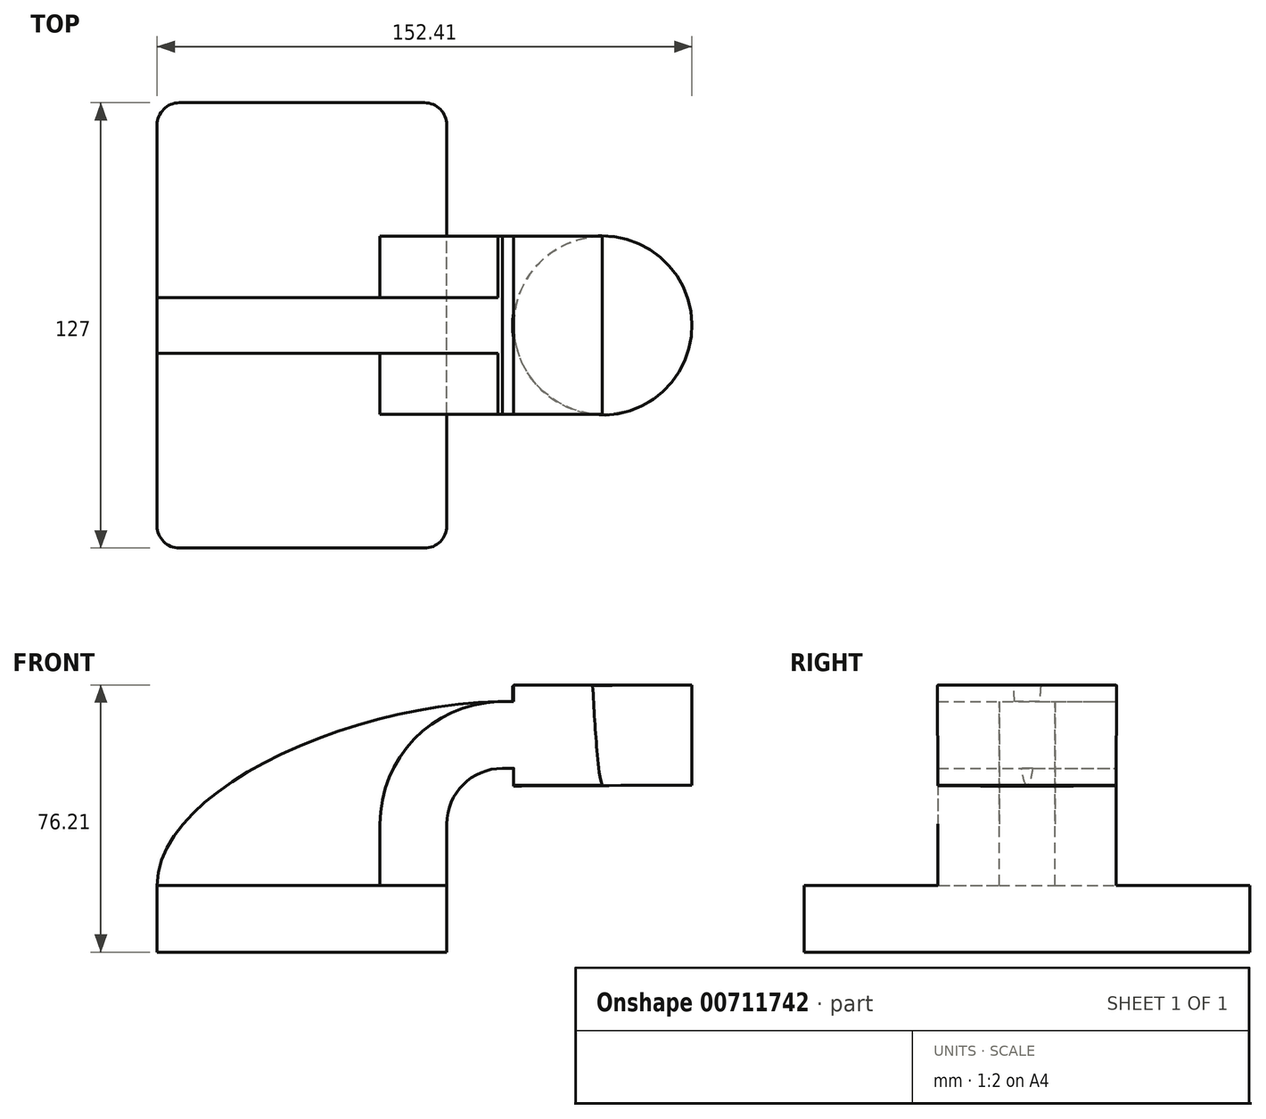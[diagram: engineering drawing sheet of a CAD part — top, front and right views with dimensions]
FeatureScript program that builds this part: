
annotation { "Feature Type Name" : "Feature", "Feature Type Description" : "" }
export const myFeature = defineFeature(function(context is Context, id is Id, definition is map)
    precondition{}
    {
        {
            var Q0;
            Q0=qCreatedBy(makeId("Front.planeOp"),FACE);
            var sketch = newSketch(context, id + "F0", { "sketchPlane" : qUnion([Q0])});
            skLineSegment(sketch, "E0.bottom", {"start": v(-41.28, -9.52) * mm, "end": v(41.28, -9.52) * mm});
            skLineSegment(sketch, "E0.top", {"start": v(-41.28, 9.52) * mm, "end": v(41.28, 9.52) * mm});
            skLineSegment(sketch, "E0.left", {"start": v(-41.28, -9.52) * mm, "end": v(-41.28, 9.52) * mm});
            skLineSegment(sketch, "E0.right", {"start": v(41.28, -9.52) * mm, "end": v(41.28, 9.52) * mm});
            skPoint(sketch, "E0.middle", {"position": v(0, 0) * mm});
            skLineSegment(sketch, "E1.bottom", {"start": v(60.33, 38.1) * mm, "end": v(111.12, 38.1) * mm});
            skLineSegment(sketch, "E1.top", {"start": v(60.33, 66.68) * mm, "end": v(111.12, 66.68) * mm});
            skLineSegment(sketch, "E1.left", {"start": v(60.33, 38.1) * mm, "end": v(60.32, 66.68) * mm});
            skLineSegment(sketch, "E1.right", {"start": v(111.12, 38.1) * mm, "end": v(111.12, 66.68) * mm});
            skPoint(sketch, "E1.middle", {"position": v(85.72, 52.39) * mm});
            skLineSegment(sketch, "E2", {"start": v(41.27, 9.52) * mm, "end": v(41.27, 27) * mm});
            skArc(sketch, "E3", {"start": v(41.27, 27) * mm, "mid": v(45.92, 38.23) * mm, "end": v(57.15, 42.88) * mm});
            skLineSegment(sketch, "E4", {"start": v(57.15, 42.88) * mm, "end": v(85.58, 42.88) * mm});
            skLineSegment(sketch, "E5.0", {"start": v(57.15, 61.93) * mm, "end": v(85.58, 61.93) * mm});
            skArc(sketch, "E5.1", {"start": v(22.23, 27) * mm, "mid": v(32.45, 51.7) * mm, "end": v(57.15, 61.93) * mm});
            skLineSegment(sketch, "E5.2", {"start": v(22.22, 9.52) * mm, "end": v(22.22, 27) * mm});
            skLineSegment(sketch, "E6", {"start": v(85.72, 38.1) * mm, "end": v(85.58, 66.68) * mm});
            skFitSpline(sketch, "E7", {"points": [v(-41.28, 9.53) * mm, v(57.15, 61.93) * mm], "startDerivative": vector(1.41, 83.98) * mm, "endDerivative": vector(126.93, 1.68) * mm});
            skSolve(sketch);
        }
        {
            var Q0;
            Q0=makeQuery(id+"F0.imprint","IMPRINT",FACE,{"disambiguationData":[TD([[makeQuery(id+"F0.imprint","IMPRINT",EDGE,{"derivedFrom":sQuery(id+"F0.wireOp",EDGE,"E0.bottom")}),1.0]])]});
            extrude(context, id + "F1", {"entities" : qUnion([Q0]), "endBound" : BoundingType.SYMMETRIC, "depth" : 127 * mm, "offsetDistance" : 25.4 * mm});
        }
        {
            var Q0;
            {var subQ1=sQuery(id+"F0.wireOp",EDGE,"E2");Q0=makeQuery(id+"F0.imprint","IMPRINT",FACE,{"disambiguationData":[TD([[makeQuery(id+"F0.imprint","IMPRINT",EDGE,{"derivedFrom":subQ1}),1.0]])]});}
            var Q1;
            {var subQ4=sQuery(id+"F0.wireOp",EDGE,"E6");Q1=makeQuery(id+"F0.imprint","IMPRINT",FACE,{"disambiguationData":[TD([[makeQuery(id+"F0.imprint","IMPRINT",EDGE,{"derivedFrom":subQ4}),1.0]])]});}
            extrude(context, id + "F2", {"entities" : qUnion([Q0, Q1]), "operationType" : NewBodyOperationType.ADD, "endBound" : BoundingType.SYMMETRIC, "depth" : 50.8 * mm, "offsetDistance" : 25.4 * mm});
        }
        {
            var Q0;
            {var subQ3=sQuery(id+"F0.wireOp",EDGE,"E5.2");Q0=makeQuery(id+"F0.imprint","IMPRINT",FACE,{"disambiguationData":[TD([[makeQuery(id+"F0.imprint","IMPRINT",EDGE,{"derivedFrom":subQ3}),1.0]])]});}
            extrude(context, id + "F3", {"entities" : qUnion([Q0]), "operationType" : NewBodyOperationType.ADD, "endBound" : BoundingType.SYMMETRIC, "depth" : 15.88 * mm, "offsetDistance" : 25.4 * mm});
        }
        {
            var Q0;
            {var subQ0=sQuery(id+"F0.wireOp",EDGE,"E1.right");Q0=makeQuery(id+"F0.imprint","IMPRINT",FACE,{"disambiguationData":[TD([[makeQuery(id+"F0.imprint","IMPRINT",EDGE,{"derivedFrom":subQ0}),1.0]])]});}
            var Q1;
            Q1=sQuery(id+"F0.wireOp",EDGE,"E6");
            revolve(context, id + "F4", {"operationType" : NewBodyOperationType.ADD, "surfaceOperationType" : NewSurfaceOperationType.NEW, "entities" : qUnion([Q0]), "axis" : qUnion([Q1]), "revolveType" : RevolveType.FULL});
        }
        {
            var Q0;
            Q0=makeQuery(id+"F1.opExtrude","CAP_EDGE",EDGE,{"disambiguationData":[OSD([sQuery(id+"F0.wireOp",EDGE,"E0.left")])],"isStart":false});
            var Q1;
            Q1=makeQuery(id+"F1.opExtrude","CAP_EDGE",EDGE,{"disambiguationData":[OSD([sQuery(id+"F0.wireOp",EDGE,"E0.right")])],"isStart":false});
            var Q2;
            Q2=makeQuery(id+"F1.opExtrude","CAP_EDGE",EDGE,{"disambiguationData":[OSD([sQuery(id+"F0.wireOp",EDGE,"E0.right")])],"isStart":true});
            var Q3;
            Q3=makeQuery(id+"F1.opExtrude","CAP_EDGE",EDGE,{"disambiguationData":[OSD([sQuery(id+"F0.wireOp",EDGE,"E0.left")])],"isStart":true});
            fillet(context, id + "F5", {"entities" : qUnion([Q0, Q1, Q2, Q3]), "radius" : 6.35 * mm, "tangentPropagation" : true, "allowEdgeOverflow" : false});
        }
    });
